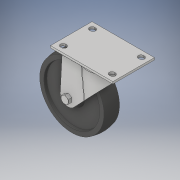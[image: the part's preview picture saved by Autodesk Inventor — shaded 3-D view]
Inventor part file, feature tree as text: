
AUTODESK INVENTOR PART (.ipt)
format: ipt  version: 2018.2 (Build 222227000, 227)  size: 360,448 bytes
history: native  units: in
note: dims shown in document units (in); Inventor stores cm internally (conversion verified against a paired STEP export)
features: revolve x1, boolean_combine x1
ambient origin geometry x8: Origin, YZ Plane, XZ Plane, XY Plane, X Axis, Y Axis, Z Axis, Center Point
bodies: Solid1 (feature_tree), Solid2 (feature_tree)
feature tree (2):
  revolve  "Revolve1"  [1 undecoded]
  boolean_combine  "Combine2"
note: 1 required parameter value undecoded (feature->parameter linkage not recoverable at this tier; creation-order binding heuristic only, values carry confidence <= 0.55)
